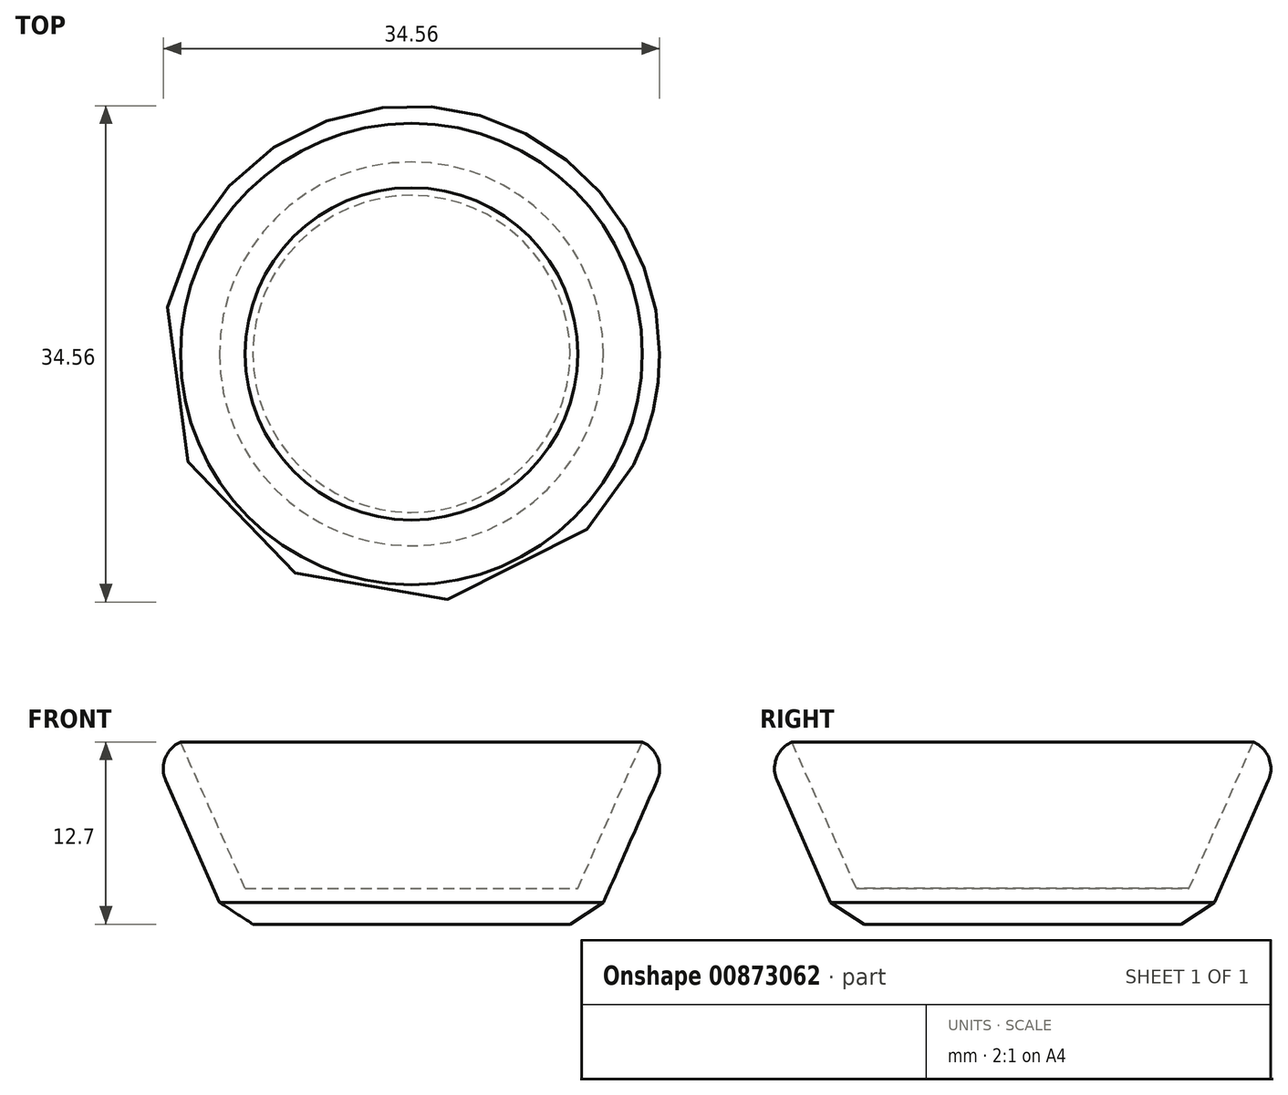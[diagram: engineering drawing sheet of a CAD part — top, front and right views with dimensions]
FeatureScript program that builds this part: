
annotation { "Feature Type Name" : "Feature", "Feature Type Description" : "" }
export const myFeature = defineFeature(function(context is Context, id is Id, definition is map)
    precondition{}
    {
        {
            var Q0;
            Q0=qCreatedBy(makeId("Front.planeOp"),FACE);
            var sketch = newSketch(context, id + "F0", { "sketchPlane" : qUnion([Q0])});
            skLineSegment(sketch, "E0", {"start": v(0, 0) * mm, "end": v(12.7, 0) * mm});
            skLineSegment(sketch, "E1", {"start": v(12.7, 0) * mm, "end": v(18.3, 12.7) * mm});
            skLineSegment(sketch, "E2", {"start": v(16.07, 12.7) * mm, "end": v(11.58, 2.48) * mm});
            skLineSegment(sketch, "E3", {"start": v(11.58, 2.48) * mm, "end": v(0, 2.48) * mm});
            skLineSegment(sketch, "E4", {"start": v(0, 2.48) * mm, "end": v(11.58, 2.48) * mm});
            skLineSegment(sketch, "E5", {"start": v(0, 0) * mm, "end": v(0, 21.11) * mm, "construction": true});
            skLineSegment(sketch, "E6", {"start": v(16.07, 12.7) * mm, "end": v(18.3, 12.7) * mm});
            skLineSegment(sketch, "E7", {"start": v(0, 2.48) * mm, "end": v(0, 0) * mm});
            skSolve(sketch);
        }
        {
            var Q0;
            Q0=makeQuery(id+"F0.imprint","IMPRINT",FACE,{"disambiguationData":[TD([[makeQuery(id+"F0.imprint","IMPRINT",EDGE,{"derivedFrom":sQuery(id+"F0.wireOp",EDGE,"E0")}),1.0]])]});
            var Q1;
            Q1=sQuery(id+"F0.wireOp",EDGE,"E5");
            revolve(context, id + "F1", {"surfaceOperationType" : NewSurfaceOperationType.NEW, "entities" : qUnion([Q0]), "axis" : qUnion([Q1]), "revolveType" : RevolveType.FULL});
        }
        {
            var Q0;
            Q0=makeQuery(id+"F1.opRevolve","SWEPT_EDGE",EDGE,{"disambiguationData":[OSD([sQuery(id+"F0.wireOp",EDGE,"E1"),sQuery(id+"F0.wireOp",EDGE,"E6")])]});
            fillet(context, id + "F2", {"entities" : qUnion([Q0]), "radius" : 2.05 * mm, "tangentPropagation" : true, "allowEdgeOverflow" : false});
        }
        {
            var Q0;
            Q0=makeQuery(id+"F1.opRevolve","SWEPT_EDGE",EDGE,{"disambiguationData":[OSD([sQuery(id+"F0.wireOp",EDGE,"E0"),sQuery(id+"F0.wireOp",EDGE,"E1")])]});
            chamfer(context, id + "F3", {"entities" : qUnion([Q0]), "width" : 2.54 * mm, "tangentPropagation" : true});
        }
    });
